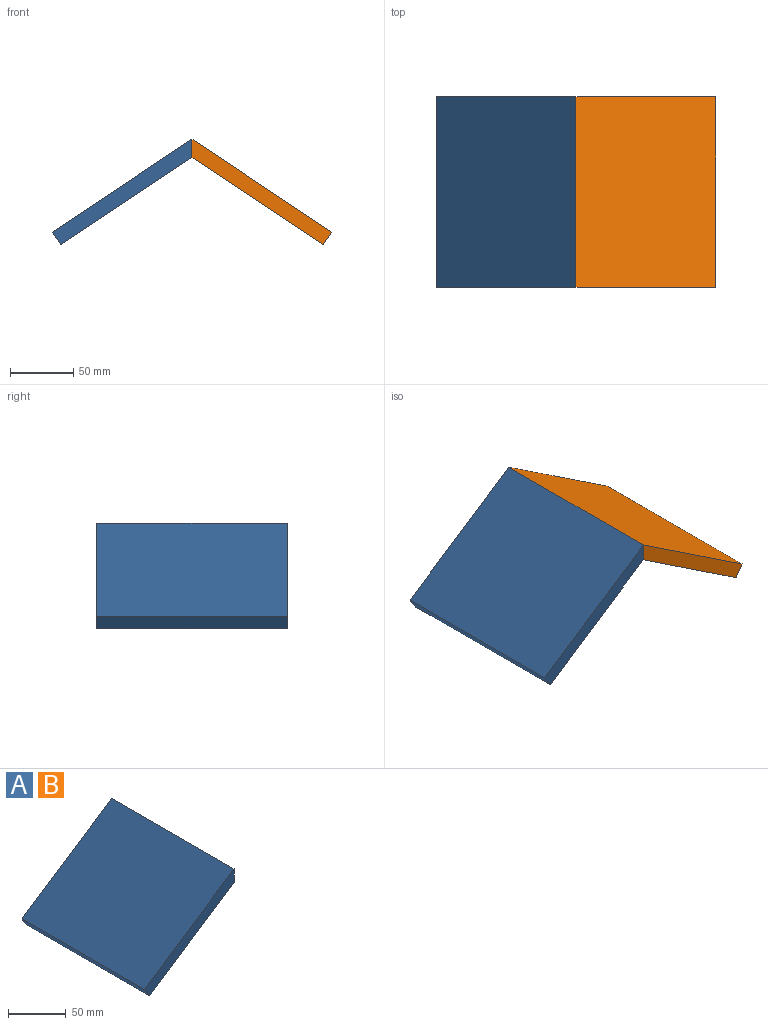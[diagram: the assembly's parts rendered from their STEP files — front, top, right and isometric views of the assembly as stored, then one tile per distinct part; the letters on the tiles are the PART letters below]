
ASSEMBLY  parts=2 mates=1
PART A: 6 faces, bbox 110x150x83.2 mm
  f0: plane 150x14.31mm, normal (1,0,0), area 2146.8mm2, adj f1,f3,f4,f5
  f1: plane 150x109.97mm, normal (-0.55,0,0.83), area 19824.9mm2, adj f0,f2,f4,f5
  f2: plane 150x9.91mm, normal (-0.83,0,-0.55), area 1786.2mm2, adj f1,f3,f4,f5
  f3: plane 150x103.36mm, normal (0.55,0,-0.83), area 18634.1mm2, adj f0,f2,f4,f5
  f4: plane 109.97x83.22mm, normal (0,-1,0), area 1526.6mm2, adj f0,f1,f2,f3
  f5: plane 109.97x83.22mm, normal (0,1,0), area 1526.6mm2, adj f0,f1,f2,f3
PART B: same geometry as A
PLACE A t=(118,-51,-14)mm
PLACE B rot(axis=(0,0,-1),180deg) t=(118,-201,-14)mm
MATE fastened B.f0 <-> A.f0  axis (-1,0,0) through (118,-126,143.16)mm
